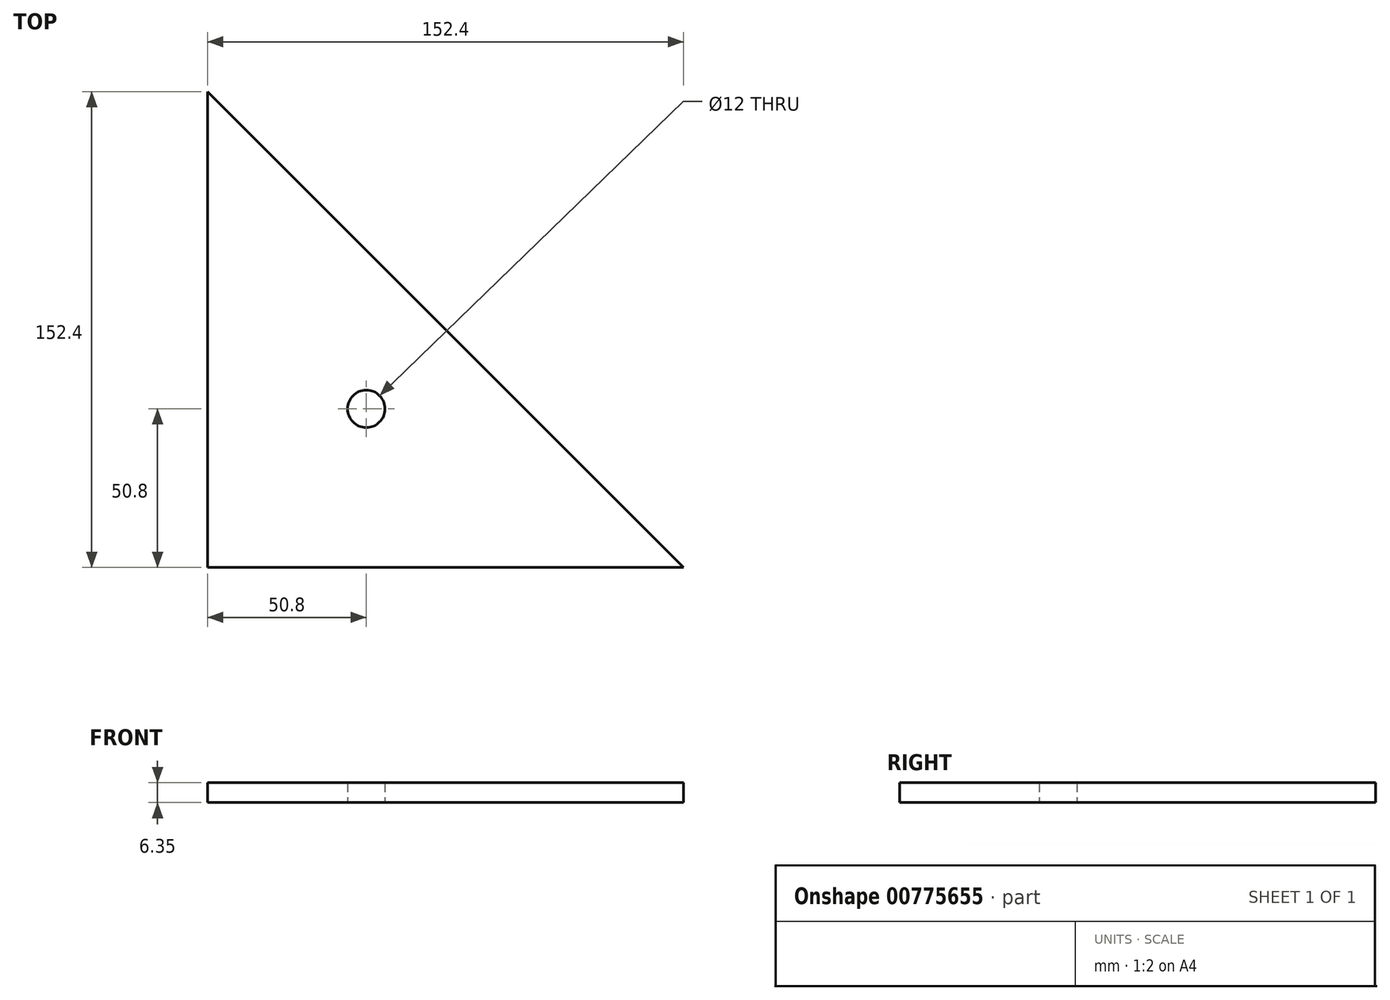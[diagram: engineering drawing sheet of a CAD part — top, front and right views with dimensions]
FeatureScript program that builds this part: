
annotation { "Feature Type Name" : "Feature", "Feature Type Description" : "" }
export const myFeature = defineFeature(function(context is Context, id is Id, definition is map)
    precondition{}
    {
        {
            var Q0;
            Q0=qCreatedBy(makeId("Top.planeOp"),FACE);
            var sketch = newSketch(context, id + "F0", { "sketchPlane" : qUnion([Q0])});
            skLineSegment(sketch, "E0", {"start": v(0, 0) * mm, "end": v(0, 152.4) * mm});
            skLineSegment(sketch, "E1", {"start": v(0, 152.4) * mm, "end": v(152.4, 0) * mm});
            skLineSegment(sketch, "E2", {"start": v(152.4, 0) * mm, "end": v(0, 0) * mm});
            skCircle(sketch, "E3", {"center": v(50.8, 50.8) * mm, "radius": 6 * mm});
            skSolve(sketch);
        }
        {
            var Q0;
            Q0=makeQuery(id+"F0.imprint","IMPRINT",FACE,{"disambiguationData":[TD([[makeQuery(id+"F0.imprint","IMPRINT",EDGE,{"derivedFrom":sQuery(id+"F0.wireOp",EDGE,"E0")}),-1.0]])]});
            extrude(context, id + "F1", {"entities" : qUnion([Q0]), "depth" : 6.35 * mm, "offsetDistance" : 25 * mm});
        }
    });
